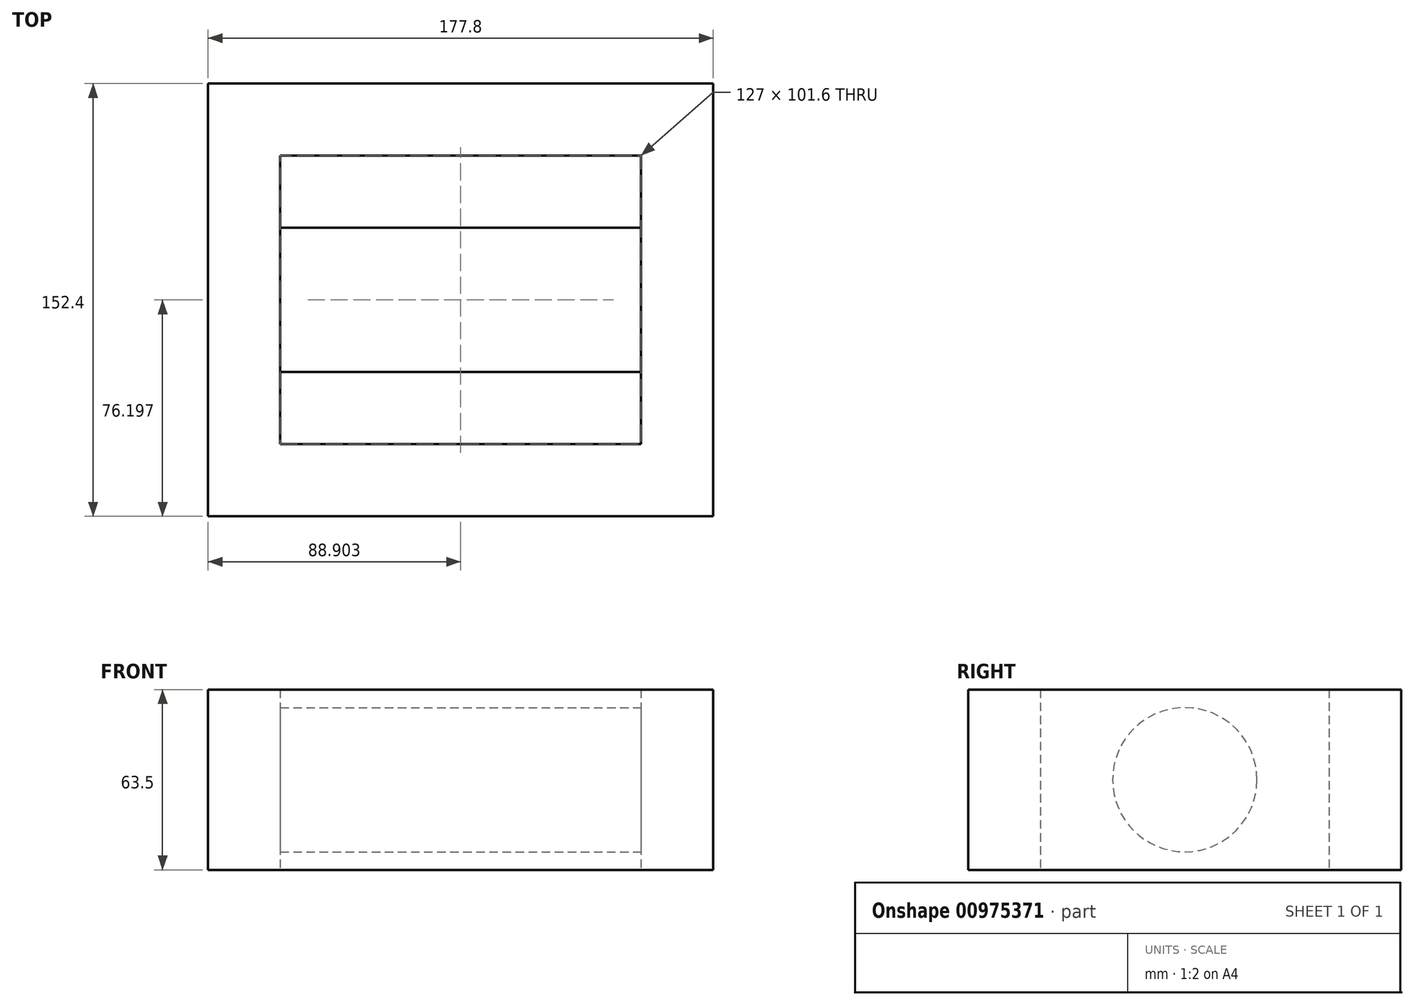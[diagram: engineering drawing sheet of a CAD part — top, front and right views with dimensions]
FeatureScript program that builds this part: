
annotation { "Feature Type Name" : "Feature", "Feature Type Description" : "" }
export const myFeature = defineFeature(function(context is Context, id is Id, definition is map)
    precondition{}
    {
        {
            var Q0;
            Q0=qCreatedBy(makeId("Top.planeOp"),FACE);
            var sketch = newSketch(context, id + "F0", { "sketchPlane" : qUnion([Q0])});
            skLineSegment(sketch, "E0", {"start": v(-76.36, 86.03) * mm, "end": v(101.44, 86.03) * mm});
            skLineSegment(sketch, "E1", {"start": v(-76.36, 86.03) * mm, "end": v(-76.36, -66.37) * mm});
            skLineSegment(sketch, "E2", {"start": v(101.44, 86.03) * mm, "end": v(101.44, -66.37) * mm});
            skLineSegment(sketch, "E3", {"start": v(101.44, -66.37) * mm, "end": v(101.44, -66.37) * mm});
            skLineSegment(sketch, "E4", {"start": v(-76.36, -66.37) * mm, "end": v(101.44, -66.37) * mm});
            skLineSegment(sketch, "E5", {"start": v(-50.96, -40.97) * mm, "end": v(-50.96, 60.63) * mm});
            skLineSegment(sketch, "E6", {"start": v(-50.96, -40.97) * mm, "end": v(76.04, -40.97) * mm});
            skLineSegment(sketch, "E7", {"start": v(76.04, -40.97) * mm, "end": v(76.04, 60.63) * mm});
            skLineSegment(sketch, "E8", {"start": v(-50.96, 60.63) * mm, "end": v(76.04, 60.63) * mm});
            skSolve(sketch);
        }
        {
            var Q0;
            Q0=makeQuery(id+"F0.imprint","IMPRINT",FACE,{"disambiguationData":[TD([[makeQuery(id+"F0.imprint","IMPRINT",EDGE,{"derivedFrom":sQuery(id+"F0.wireOp",EDGE,"E0")}),-1.0]])]});
            extrude(context, id + "F1", {"entities" : qUnion([Q0]), "depth" : 63.5 * mm, "offsetDistance" : 25.4 * mm});
        }
        {
            var Q0;
            Q0=makeQuery(id+"F1.opExtrude","SWEPT_FACE",FACE,{"disambiguationData":[OSD([sQuery(id+"F0.wireOp",EDGE,"E7")])]});
            var sketch = newSketch(context, id + "F2", { "sketchPlane" : qUnion([Q0])});
            skCircle(sketch, "E9", {"center": v(-9.83, 31.75) * mm, "radius": 25.4 * mm});
            skSolve(sketch);
        }
        {
            var Q0;
            Q0 = qSketchRegion(id + "F2", true);
            extrude(context, id + "F3", {"entities" : qUnion([Q0]), "operationType" : NewBodyOperationType.ADD, "depth" : 143 * mm, "offsetDistance" : 25.4 * mm});
        }
    });
